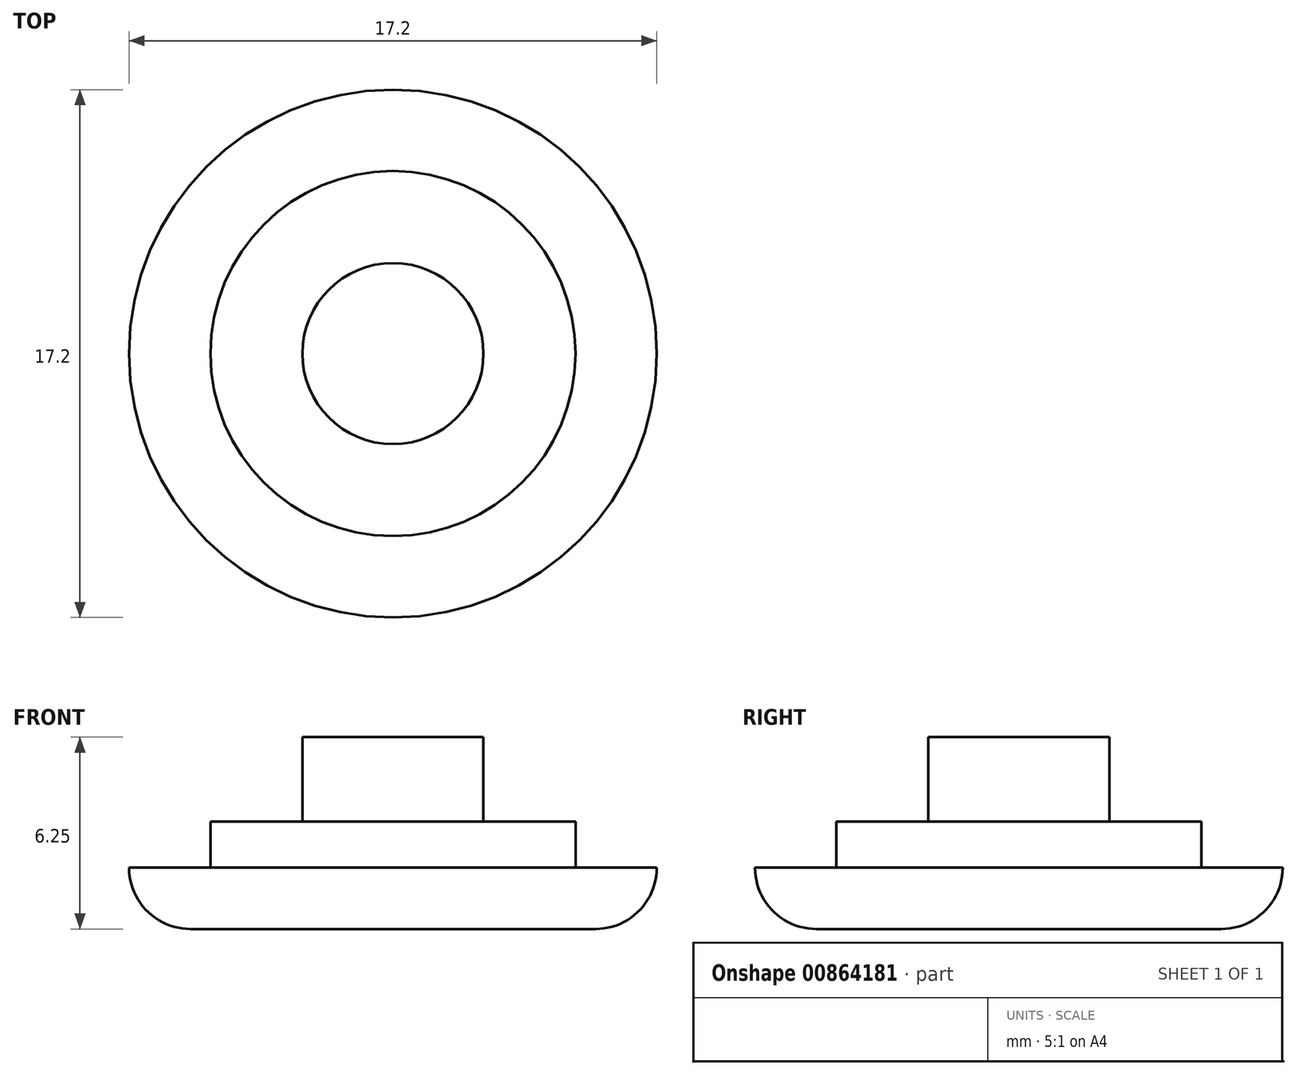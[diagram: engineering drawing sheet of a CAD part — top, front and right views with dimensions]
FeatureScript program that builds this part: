
annotation { "Feature Type Name" : "Feature", "Feature Type Description" : "" }
export const myFeature = defineFeature(function(context is Context, id is Id, definition is map)
    precondition{}
    {
        {
            var Q0;
            Q0=qCreatedBy(makeId("Top.planeOp"),FACE);
            var sketch = newSketch(context, id + "F0", { "sketchPlane" : qUnion([Q0])});
            skCircle(sketch, "E0", {"center": v(-45.62, 18.56) * mm, "radius": 8.6 * mm});
            skCircle(sketch, "E1.0", {"center": v(-45.62, 18.56) * mm, "radius": 2.95 * mm});
            skCircle(sketch, "E2.0", {"center": v(-45.62, 18.56) * mm, "radius": 5.95 * mm});
            skSolve(sketch);
        }
        {
            var Q0;
            Q0=makeQuery(id+"F0.imprint","IMPRINT",FACE,{"disambiguationData":[TD([[makeQuery(id+"F0.imprint","IMPRINT",EDGE,{"derivedFrom":sQuery(id+"F0.wireOp",EDGE,"E0")}),1.0]])]});
            extrude(context, id + "F1", {"entities" : qUnion([Q0]), "depth" : 2 * mm, "offsetDistance" : 25.4 * mm});
        }
        {
            var Q0;
            Q0=makeQuery(id+"F0.imprint","IMPRINT",FACE,{"disambiguationData":[TD([[makeQuery(id+"F0.imprint","IMPRINT",EDGE,{"derivedFrom":sQuery(id+"F0.wireOp",EDGE,"E1.0")}),-1.0]])]});
            var Q1;
            Q1=makeQuery(id+"F0.imprint","IMPRINT",FACE,{"disambiguationData":[TD([[makeQuery(id+"F0.imprint","IMPRINT",EDGE,{"derivedFrom":sQuery(id+"F0.wireOp",EDGE,"HBSmemsx-eVrp-CbMX-09FM-U9VBp0o4ru2J")}),1.0]])]});
            extrude(context, id + "F2", {"entities" : qUnion([Q0, Q1]), "operationType" : NewBodyOperationType.ADD, "depth" : 3.5 * mm, "offsetDistance" : 25.4 * mm});
        }
        {
            var Q0;
            Q0=makeQuery(id+"F0.imprint","IMPRINT",FACE,{"disambiguationData":[TD([[makeQuery(id+"F0.imprint","IMPRINT",EDGE,{"derivedFrom":sQuery(id+"F0.wireOp",EDGE,"E1.0")}),1.0]])]});
            extrude(context, id + "F3", {"entities" : qUnion([Q0]), "operationType" : NewBodyOperationType.ADD, "depth" : 6.25 * mm, "offsetDistance" : 25.4 * mm});
        }
        {
            var Q0;
            Q0=makeQuery(id+"F1.opExtrude","CAP_EDGE",EDGE,{"disambiguationData":[OSD([sQuery(id+"F0.wireOp",EDGE,"E0")])],"isStart":true});
            fillet(context, id + "F4", {"entities" : qUnion([Q0]), "radius" : 2 * mm, "tangentPropagation" : true, "allowEdgeOverflow" : false});
        }
    });
